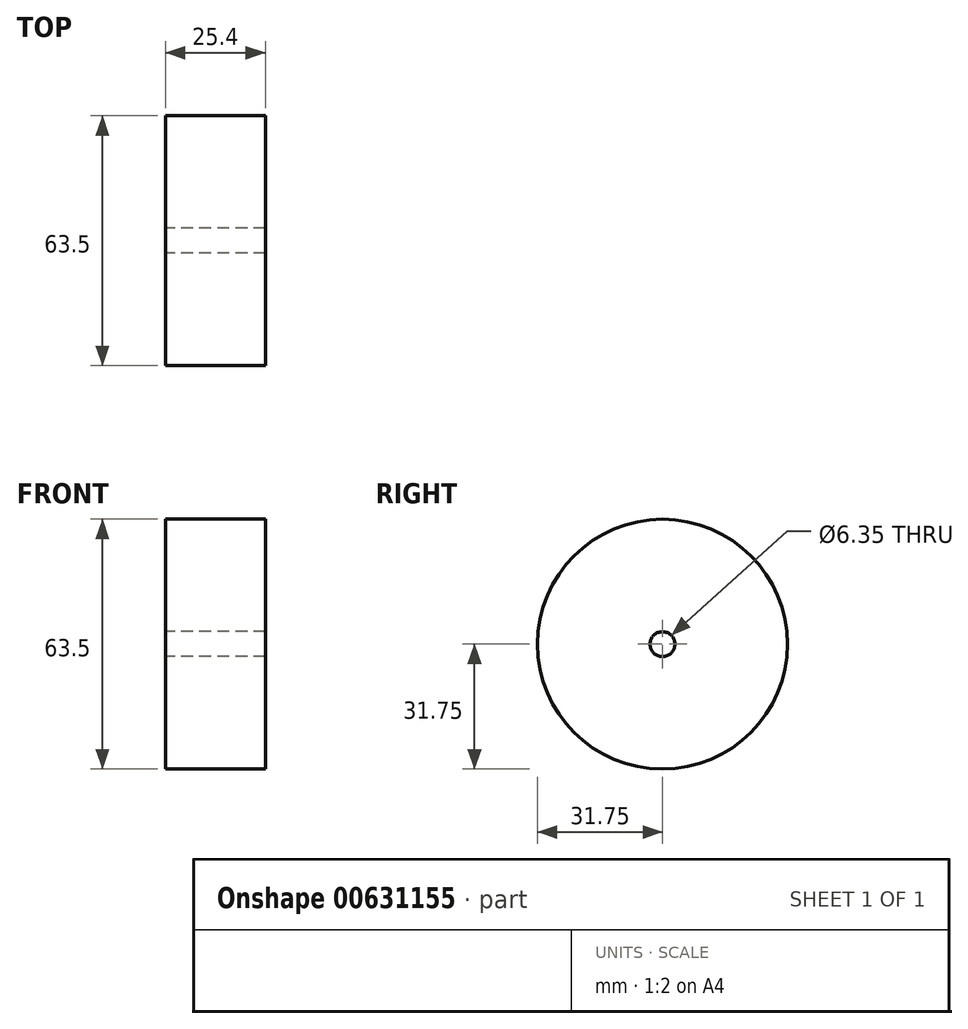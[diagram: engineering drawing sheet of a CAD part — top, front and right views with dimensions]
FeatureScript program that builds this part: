
annotation { "Feature Type Name" : "Feature", "Feature Type Description" : "" }
export const myFeature = defineFeature(function(context is Context, id is Id, definition is map)
    precondition{}
    {
        {
            var Q0;
            Q0=qCreatedBy(makeId("Right.planeOp"),FACE);
            var sketch = newSketch(context, id + "F0", { "sketchPlane" : qUnion([Q0])});
            skCircle(sketch, "E0", {"center": v(0, 0) * mm, "radius": 31.75 * mm});
            skCircle(sketch, "E1", {"center": v(0, 0) * mm, "radius": 3.18 * mm});
            skSolve(sketch);
        }
        {
            var Q0;
            Q0=makeQuery(id+"F0.imprint","IMPRINT",FACE,{"disambiguationData":[TD([[makeQuery(id+"F0.imprint","IMPRINT",EDGE,{"derivedFrom":sQuery(id+"F0.wireOp",EDGE,"E0")}),1.0]])]});
            extrude(context, id + "F1", {"entities" : qUnion([Q0]), "depth" : 25.4 * mm, "offsetDistance" : 25.4 * mm});
        }
    });
